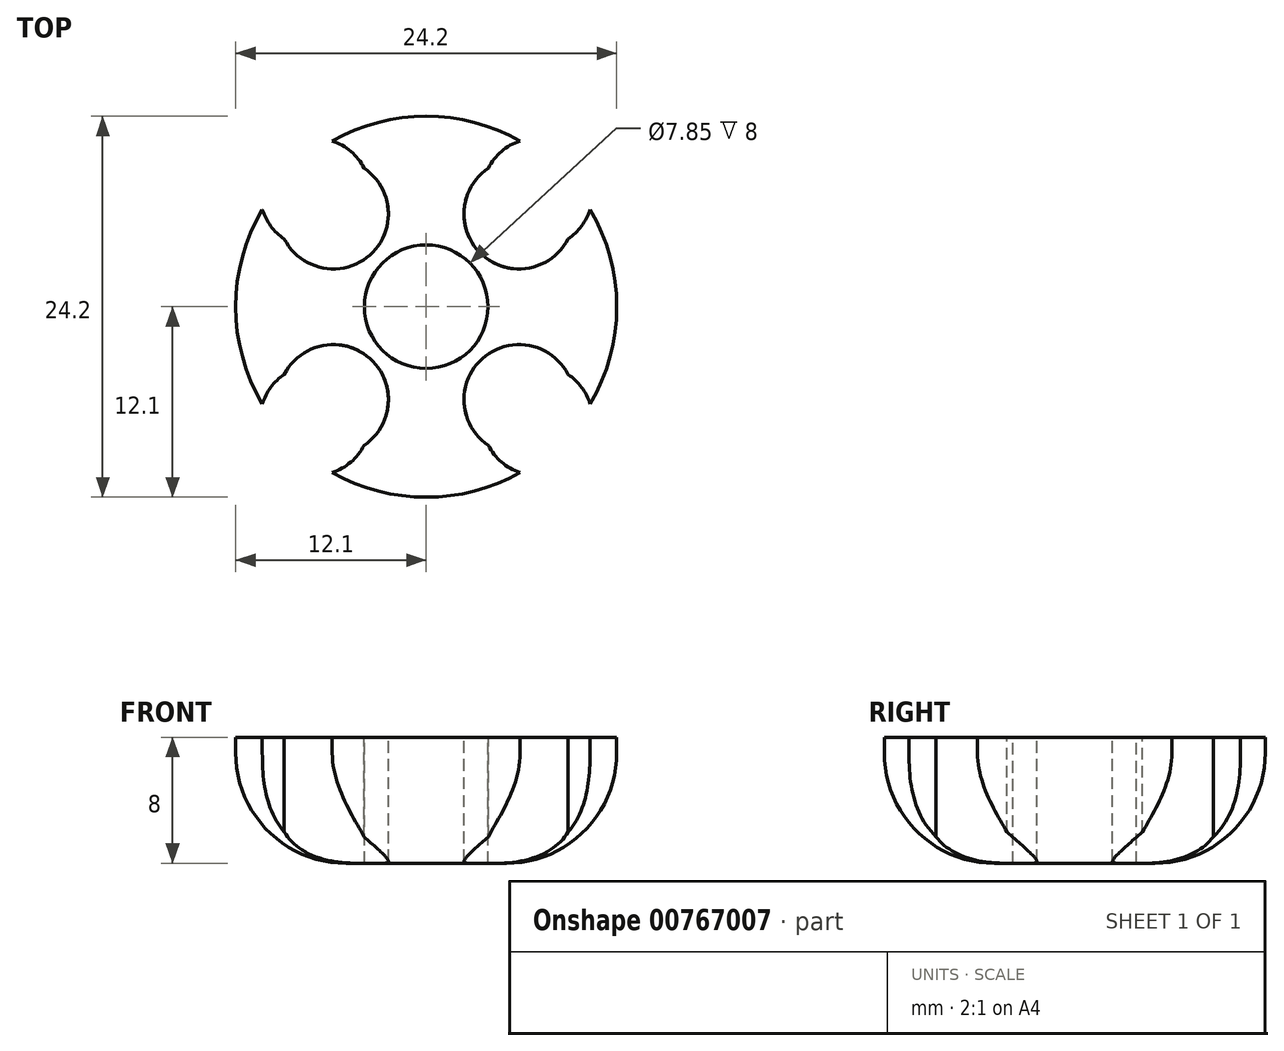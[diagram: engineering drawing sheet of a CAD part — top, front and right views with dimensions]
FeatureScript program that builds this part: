
annotation { "Feature Type Name" : "Feature", "Feature Type Description" : "" }
export const myFeature = defineFeature(function(context is Context, id is Id, definition is map)
    precondition{}
    {
        {
            var Q0;
            Q0=qCreatedBy(makeId("Top.planeOp"),FACE);
            var sketch = newSketch(context, id + "F0", { "sketchPlane" : qUnion([Q0])});
            skCircle(sketch, "E0", {"center": v(0, 0) * mm, "radius": 3.92 * mm});
            skArc(sketch, "E1", {"start": v(-5.75, 8.37) * mm, "mid": v(-8.23, 8.52) * mm, "end": v(-8.37, 6.05) * mm});
            skArc(sketch, "E2", {"start": v(-7.2, 4.74) * mm, "mid": v(-4.74, 4.6) * mm, "end": v(-4.6, 7.06) * mm});
            skLineSegment(sketch, "E3", {"start": v(0, 9.23) * mm, "end": v(0, -8.76) * mm, "construction": true});
            skLineSegment(sketch, "E4", {"start": v(-7.52, 0) * mm, "end": v(6.15, 0) * mm, "construction": true});
            skCircle(sketch, "E5", {"center": v(0, 0) * mm, "radius": 12.1 * mm});
            skLineSegment(sketch, "E6", {"start": v(-7.2, 4.74) * mm, "end": v(-8.37, 6.05) * mm});
            skLineSegment(sketch, "E7", {"start": v(-5.75, 8.37) * mm, "end": v(-4.6, 7.06) * mm});
            skLineSegment(sketch, "E8.MirrorCS", {"start": v(7.2, 4.74) * mm, "end": v(8.37, 6.05) * mm});
            skArc(sketch, "E9.MirrorCS", {"start": v(7.2, 4.74) * mm, "mid": v(4.74, 4.6) * mm, "end": v(4.6, 7.06) * mm});
            skArc(sketch, "E10.MirrorCS", {"start": v(5.75, 8.37) * mm, "mid": v(8.23, 8.52) * mm, "end": v(8.37, 6.05) * mm});
            skLineSegment(sketch, "E11.MirrorCS", {"start": v(5.75, 8.37) * mm, "end": v(4.6, 7.06) * mm});
            skLineSegment(sketch, "E12.MirrorCS", {"start": v(-7.2, -4.74) * mm, "end": v(-8.37, -6.05) * mm});
            skArc(sketch, "E13.MirrorCS", {"start": v(-5.75, -8.37) * mm, "mid": v(-8.23, -8.52) * mm, "end": v(-8.37, -6.05) * mm});
            skLineSegment(sketch, "E14.MirrorCS", {"start": v(-5.75, -8.37) * mm, "end": v(-4.6, -7.06) * mm});
            skArc(sketch, "E15.MirrorCS", {"start": v(-7.2, -4.74) * mm, "mid": v(-4.74, -4.6) * mm, "end": v(-4.6, -7.06) * mm});
            skArc(sketch, "E16.MirrorCS", {"start": v(7.2, -4.74) * mm, "mid": v(4.74, -4.6) * mm, "end": v(4.6, -7.06) * mm});
            skLineSegment(sketch, "E17.MirrorCS", {"start": v(5.75, -8.37) * mm, "end": v(4.6, -7.06) * mm});
            skArc(sketch, "E18.MirrorCS", {"start": v(5.75, -8.37) * mm, "mid": v(8.23, -8.52) * mm, "end": v(8.37, -6.05) * mm});
            skLineSegment(sketch, "E19.MirrorCS", {"start": v(7.2, -4.74) * mm, "end": v(8.37, -6.05) * mm});
            skSolve(sketch);
        }
        {
            var Q0;
            Q0=makeQuery(id+"F0.imprint","IMPRINT",FACE,{"disambiguationData":[TD([[makeQuery(id+"F0.imprint","IMPRINT",EDGE,{"derivedFrom":sQuery(id+"F0.wireOp",EDGE,"E0")}),-1.0]])]});
            extrude(context, id + "F1", {"entities" : qUnion([Q0]), "oppositeDirection" : true, "depth" : 8 * mm, "offsetDistance" : 25 * mm});
        }
        {
            var Q0;
            Q0=sQuery(id+"F0.wireOp",VERTEX,"ed581767-63f2-4939-89f5-38e3075450300.MirrorCS.center");
            var Q1;
            Q1=sQuery(id+"F0.wireOp",VERTEX,"b49008e6-ddf1-487d-8f2b-f4084e0e80c00.MirrorCS.center");
            var Q2;
            Q2=sQuery(id+"F0.wireOp",VERTEX,"e278ef37-eafc-4f3b-8837-cecc8acec1d50.MirrorCS.center");
            var Q3;
            Q3=sQuery(id+"F0.wireOp",VERTEX,"ec7a1130-b445-4bdb-86b6-875601b07efc0.MirrorCS.center");
            var Q4;
            Q4=sQuery(id+"F0.wireOp",VERTEX,"07867c65-a2c5-416c-afed-1355940a778a0.MirrorCS.center");
            var Q5;
            Q5=sQuery(id+"F0.wireOp",VERTEX,"d9cc334f-38a8-4218-b7d5-a95f48bd52030.MirrorCS.center");
            var Q6;
            Q6=sQuery(id+"F0.wireOp",VERTEX,"E2.center");
            var Q7;
            Q7=sQuery(id+"F0.wireOp",VERTEX,"E1.center");
            var Q8;
            Q8=sQuery(id+"F0.wireOp",VERTEX,"E13.MirrorCS.center");
            var Q9;
            Q9=sQuery(id+"F0.wireOp",VERTEX,"E18.MirrorCS.center");
            var Q10;
            Q10=sQuery(id+"F0.wireOp",VERTEX,"E16.MirrorCS.center");
            var Q11;
            Q11=sQuery(id+"F0.wireOp",VERTEX,"E9.MirrorCS.center");
            var Q12;
            Q12=sQuery(id+"F0.wireOp",VERTEX,"E10.MirrorCS.center");
            var Q13;
            Q13=sQuery(id+"F0.wireOp",VERTEX,"E15.MirrorCS.center");
            var Q14;
            Q14=makeQuery(id+"F1.opExtrude","SWEPT_BODY",BODY,{"disambiguationData":[OSD([sQuery(id+"F0.wireOp",EDGE,"E0"),sQuery(id+"F0.wireOp",EDGE,"E1"),sQuery(id+"F0.wireOp",EDGE,"E2"),sQuery(id+"F0.wireOp",EDGE,"b49008e6-ddf1-487d-8f2b-f4084e0e80c00.MirrorCS"),sQuery(id+"F0.wireOp",EDGE,"ed581767-63f2-4939-89f5-38e3075450300.MirrorCS"),sQuery(id+"F0.wireOp",EDGE,"07867c65-a2c5-416c-afed-1355940a778a0.MirrorCS"),sQuery(id+"F0.wireOp",EDGE,"d9cc334f-38a8-4218-b7d5-a95f48bd52030.MirrorCS"),sQuery(id+"F0.wireOp",EDGE,"ec7a1130-b445-4bdb-86b6-875601b07efc0.MirrorCS"),sQuery(id+"F0.wireOp",EDGE,"e278ef37-eafc-4f3b-8837-cecc8acec1d50.MirrorCS"),sQuery(id+"F0.wireOp",EDGE,"E5")])]});
            hole(context, id + "F2", {"style" : HoleStyle.C_BORE, "endStyle" : HoleEndStyle.BLIND, "holeDiameter" : 5 * mm, "cBoreDiameter" : 7 * mm, "cBoreDepth" : 9 * mm, "majorDiameter" : 5 * mm, "holeDepth" : 12 * mm, "isTappedThrough" : true, "tappedDepth" : 12 * mm, "tapClearance" : 3, "locations" : qUnion([Q0, Q1, Q2, Q3, Q4, Q5, Q6, Q7, Q8, Q9, Q10, Q11, Q12, Q13]), "scope" : qUnion([Q14])});
        }
        {
            var Q0;
            {var subQ0=sQuery(id+"F0.wireOp",EDGE,"E5");var subQ3=makeQuery(id+"F2.hole-3.opRevolve","SWEPT_FACE",FACE,{"disambiguationData":[OSD([sQuery(id+"F2.hole-3.sketch.wireOp",EDGE,"cbore_start_line_2")])]});var subQ5=makeQuery(id+"F2.hole-1.boolean.opBoolean","COPY",FACE,{"disambiguationData":[OD(1.0)],"derivedFrom":makeQuery(id+"F2.hole-1.opRevolve","SWEPT_FACE",FACE,{"disambiguationData":[OSD([sQuery(id+"F2.hole-1.sketch.wireOp",EDGE,"cbore_start_line_2")])]})});var subQ6=makeQuery(id+"F2.hole-2.opRevolve","SWEPT_FACE",FACE,{"disambiguationData":[OSD([sQuery(id+"F2.hole-2.sketch.wireOp",EDGE,"cbore_start_line_2")])]});var subQ7=makeQuery(id+"F2.hole-2.boolean.opBoolean","SPLIT",EDGE,{"disambiguationData":[TD([subQ5])],"derivedFrom":makeQuery(id+"F1.opExtrude","CAP_EDGE",EDGE,{"disambiguationData":[OSD([subQ0])],"isStart":false})});var subQ8=makeQuery(id+"F2.hole-3.boolean.opBoolean","SPLIT",EDGE,{"disambiguationData":[TD([subQ5])],"derivedFrom":subQ7});Q0=qUnion([makeQuery(id+"F2.hole-3.boolean.opBoolean","SPLIT",EDGE,{"disambiguationData":[TD([makeQuery(id+"F2.hole-2.boolean.opBoolean","COPY",FACE,{"derivedFrom":subQ6})])],"derivedFrom":subQ7}),makeQuery(id+"F2.hole-6.boolean.opBoolean","SPLIT",EDGE,{"disambiguationData":[TD([subQ5])],"derivedFrom":subQ8}),makeQuery(id+"F2.hole-6.boolean.opBoolean","SPLIT",EDGE,{"disambiguationData":[TD([makeQuery(id+"F2.hole-3.boolean.opBoolean","COPY",FACE,{"derivedFrom":subQ3})])],"derivedFrom":subQ8})]);}
            var Q1;
            {var subQ0=sQuery(id+"F0.wireOp",EDGE,"E5");var subQ3=makeQuery(id+"F2.hole-3.opRevolve","SWEPT_FACE",FACE,{"disambiguationData":[OSD([sQuery(id+"F2.hole-3.sketch.wireOp",EDGE,"cbore_start_line_2")])]});var subQ5=makeQuery(id+"F2.hole-1.boolean.opBoolean","COPY",FACE,{"disambiguationData":[OD(1.0)],"derivedFrom":makeQuery(id+"F2.hole-1.opRevolve","SWEPT_FACE",FACE,{"disambiguationData":[OSD([sQuery(id+"F2.hole-1.sketch.wireOp",EDGE,"cbore_start_line_2")])]})});var subQ6=makeQuery(id+"F2.hole-2.opRevolve","SWEPT_FACE",FACE,{"disambiguationData":[OSD([sQuery(id+"F2.hole-2.sketch.wireOp",EDGE,"cbore_start_line_2")])]});var subQ7=makeQuery(id+"F2.hole-2.boolean.opBoolean","SPLIT",EDGE,{"disambiguationData":[TD([subQ5])],"derivedFrom":makeQuery(id+"F1.opExtrude","CAP_EDGE",EDGE,{"disambiguationData":[OSD([subQ0])],"isStart":false})});var subQ8=makeQuery(id+"F2.hole-3.boolean.opBoolean","SPLIT",EDGE,{"disambiguationData":[TD([subQ5])],"derivedFrom":subQ7});Q1=qUnion([makeQuery(id+"F2.hole-3.boolean.opBoolean","SPLIT",EDGE,{"disambiguationData":[TD([makeQuery(id+"F2.hole-2.boolean.opBoolean","COPY",FACE,{"derivedFrom":subQ6})])],"derivedFrom":subQ7}),makeQuery(id+"F2.hole-6.boolean.opBoolean","SPLIT",EDGE,{"disambiguationData":[TD([subQ5])],"derivedFrom":subQ8}),makeQuery(id+"F2.hole-6.boolean.opBoolean","SPLIT",EDGE,{"disambiguationData":[TD([makeQuery(id+"F2.hole-3.boolean.opBoolean","COPY",FACE,{"derivedFrom":subQ3})])],"derivedFrom":subQ8})]);}
            var Q2;
            {var subQ0=sQuery(id+"F0.wireOp",EDGE,"E5");var subQ3=makeQuery(id+"F2.hole-3.opRevolve","SWEPT_FACE",FACE,{"disambiguationData":[OSD([sQuery(id+"F2.hole-3.sketch.wireOp",EDGE,"cbore_start_line_2")])]});var subQ5=makeQuery(id+"F2.hole-1.boolean.opBoolean","COPY",FACE,{"disambiguationData":[OD(1.0)],"derivedFrom":makeQuery(id+"F2.hole-1.opRevolve","SWEPT_FACE",FACE,{"disambiguationData":[OSD([sQuery(id+"F2.hole-1.sketch.wireOp",EDGE,"cbore_start_line_2")])]})});var subQ6=makeQuery(id+"F2.hole-2.opRevolve","SWEPT_FACE",FACE,{"disambiguationData":[OSD([sQuery(id+"F2.hole-2.sketch.wireOp",EDGE,"cbore_start_line_2")])]});var subQ7=makeQuery(id+"F2.hole-2.boolean.opBoolean","SPLIT",EDGE,{"disambiguationData":[TD([subQ5])],"derivedFrom":makeQuery(id+"F1.opExtrude","CAP_EDGE",EDGE,{"disambiguationData":[OSD([subQ0])],"isStart":false})});var subQ8=makeQuery(id+"F2.hole-3.boolean.opBoolean","SPLIT",EDGE,{"disambiguationData":[TD([subQ5])],"derivedFrom":subQ7});Q2=qUnion([makeQuery(id+"F2.hole-3.boolean.opBoolean","SPLIT",EDGE,{"disambiguationData":[TD([makeQuery(id+"F2.hole-2.boolean.opBoolean","COPY",FACE,{"derivedFrom":subQ6})])],"derivedFrom":subQ7}),makeQuery(id+"F2.hole-6.boolean.opBoolean","SPLIT",EDGE,{"disambiguationData":[TD([subQ5])],"derivedFrom":subQ8}),makeQuery(id+"F2.hole-6.boolean.opBoolean","SPLIT",EDGE,{"disambiguationData":[TD([makeQuery(id+"F2.hole-3.boolean.opBoolean","COPY",FACE,{"derivedFrom":subQ3})])],"derivedFrom":subQ8})]);}
            var Q3;
            {var subQ0=sQuery(id+"F0.wireOp",EDGE,"E5");Q3=makeQuery(id+"F2.hole-2.boolean.opBoolean","SPLIT",EDGE,{"disambiguationData":[TD([makeQuery(id+"F2.hole-1.boolean.opBoolean","COPY",FACE,{"disambiguationData":[OD(0.0)],"derivedFrom":makeQuery(id+"F2.hole-1.opRevolve","SWEPT_FACE",FACE,{"disambiguationData":[OSD([sQuery(id+"F2.hole-1.sketch.wireOp",EDGE,"cbore_start_line_2")])]})})])],"derivedFrom":makeQuery(id+"F1.opExtrude","CAP_EDGE",EDGE,{"disambiguationData":[OSD([subQ0])],"isStart":false})});}
            fillet(context, id + "F3", {"entities" : qUnion([Q0, Q1, Q2, Q3]), "radius" : 7 * mm, "tangentPropagation" : true, "defaultsChanged" : true, "vertexSettings" : [], "allowEdgeOverflow" : false});
        }
    });
